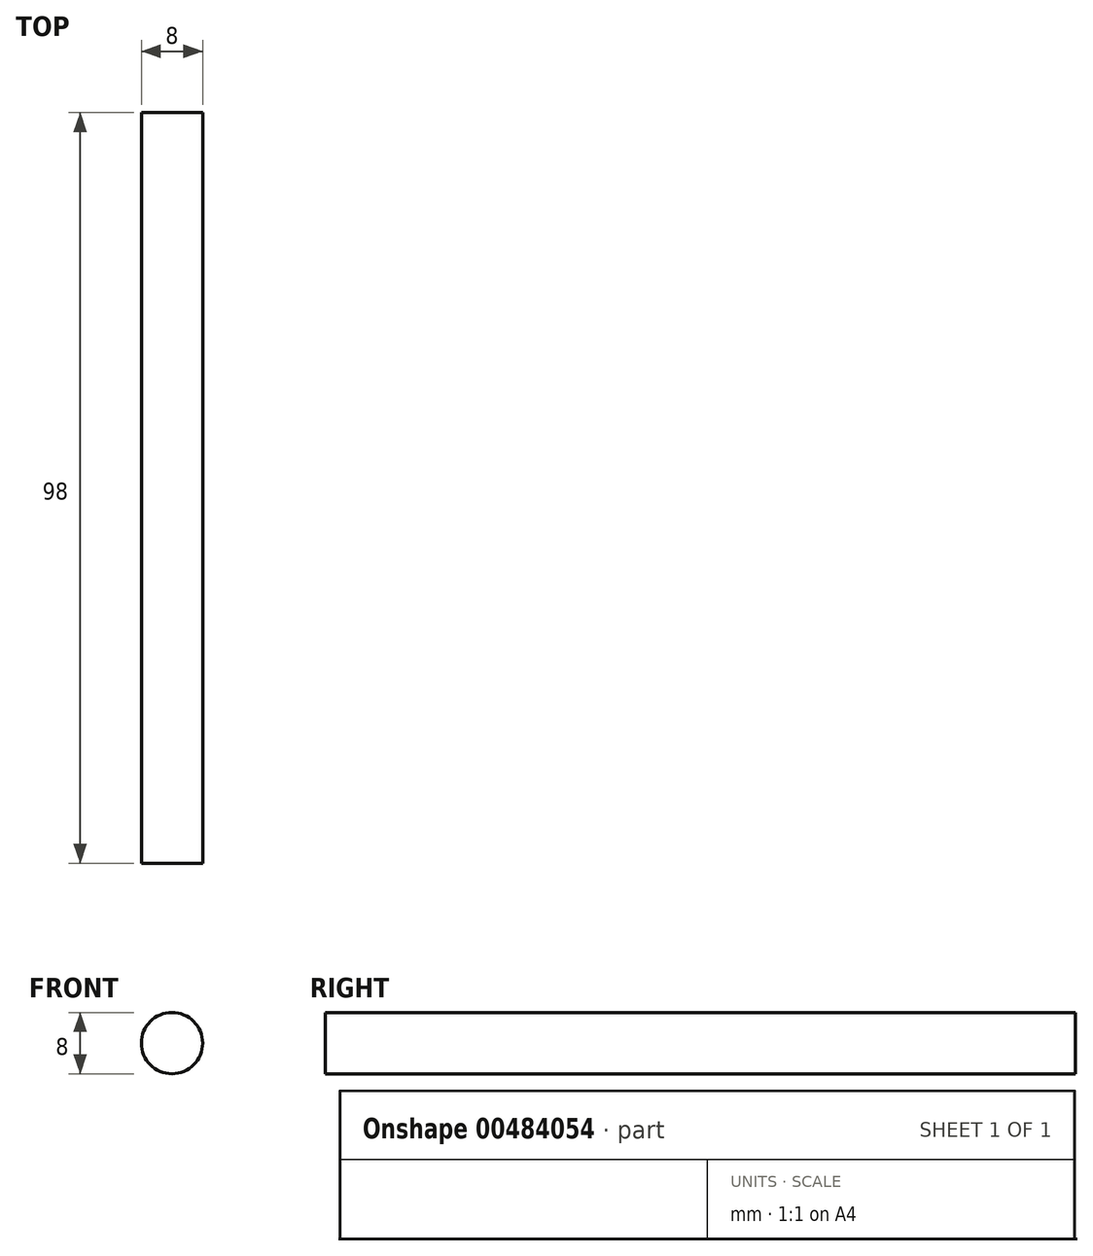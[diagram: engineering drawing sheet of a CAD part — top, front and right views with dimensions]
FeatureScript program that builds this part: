
annotation { "Feature Type Name" : "Feature", "Feature Type Description" : "" }
export const myFeature = defineFeature(function(context is Context, id is Id, definition is map)
    precondition{}
    {
        {
            var Q0;
            Q0=qCreatedBy(makeId("Front.planeOp"),FACE);
            var sketch = newSketch(context, id + "F0", { "sketchPlane" : qUnion([Q0])});
            skCircle(sketch, "E0", {"center": v(0, 0) * mm, "radius": 4 * mm});
            skSolve(sketch);
        }
        {
            var Q0;
            Q0 = qSketchRegion(id + "F0", true);
            extrude(context, id + "F1", {"entities" : qUnion([Q0]), "endBound" : BoundingType.SYMMETRIC, "depth" : 98 * mm});
        }
    });
